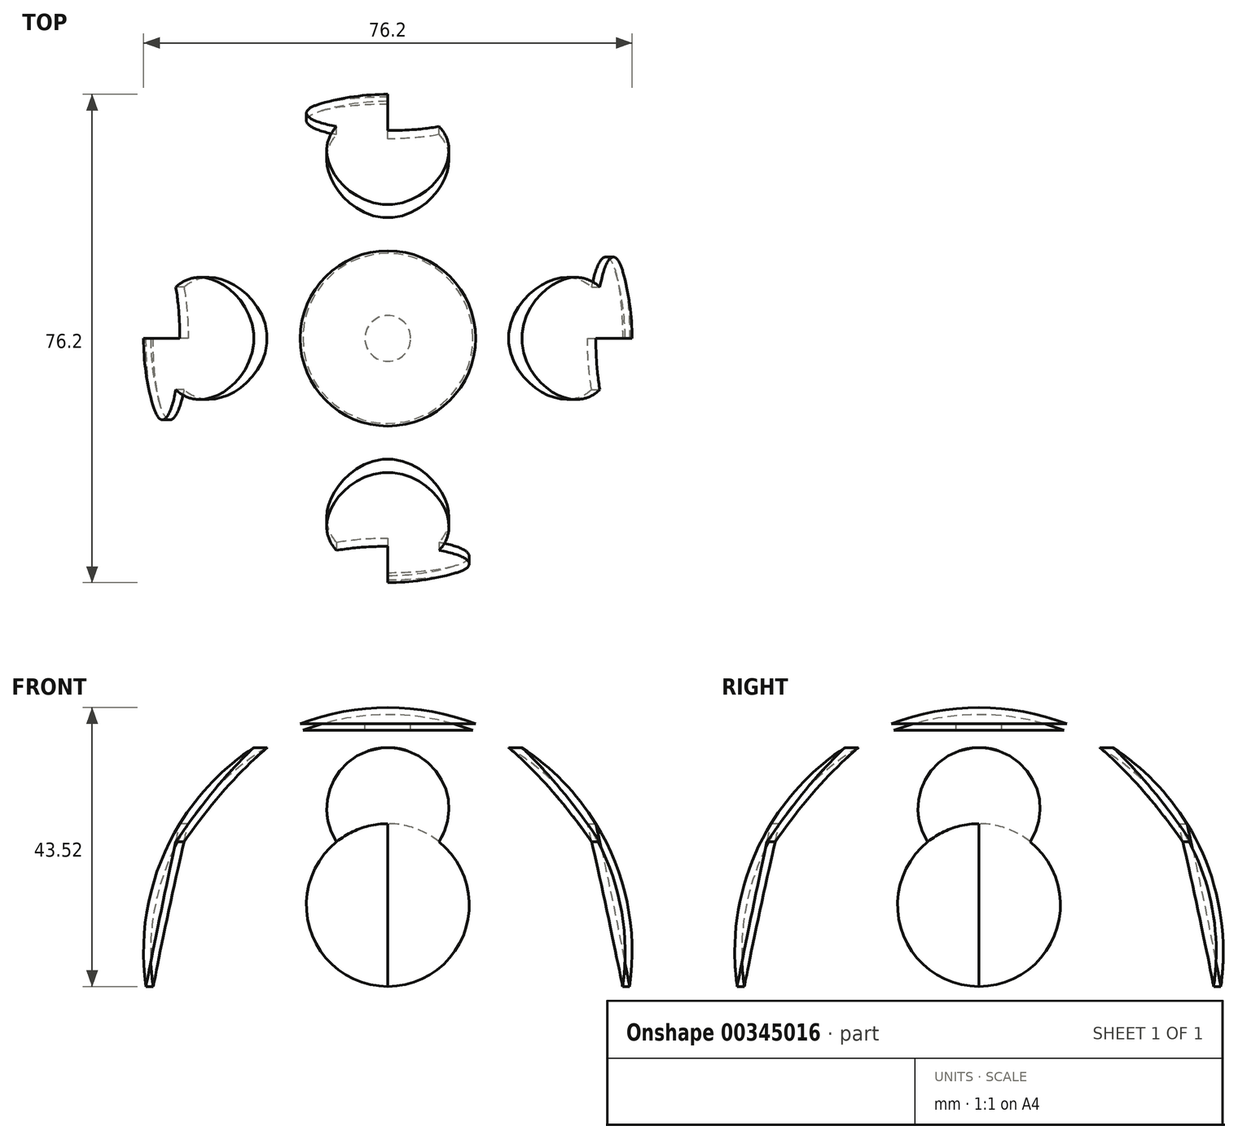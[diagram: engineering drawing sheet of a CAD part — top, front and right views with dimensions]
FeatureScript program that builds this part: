
annotation { "Feature Type Name" : "Feature", "Feature Type Description" : "" }
export const myFeature = defineFeature(function(context is Context, id is Id, definition is map)
    precondition{}
    {
        {
            var Q0;
            Q0=qCreatedBy(makeId("Top.planeOp"),FACE);
            var sketch = newSketch(context, id + "F0", { "sketchPlane" : qUnion([Q0])});
            skArc(sketch, "E0", {"start": v(0, -38.1) * mm, "mid": v(38.1, 0) * mm, "end": v(0, 38.1) * mm});
            skLineSegment(sketch, "E1", {"start": v(0, 38.1) * mm, "end": v(0, -38.1) * mm});
            skSolve(sketch);
        }
        {
            var Q0;
            Q0=makeQuery(id+"F0.imprint","IMPRINT",FACE,{"disambiguationData":[TD([[makeQuery(id+"F0.imprint","IMPRINT",EDGE,{"derivedFrom":sQuery(id+"F0.wireOp",EDGE,"E0")}),1.0]])]});
            var Q1;
            Q1=sQuery(id+"F0.wireOp",EDGE,"E1");
            revolve(context, id + "F1", {"entities" : qUnion([Q0]), "axis" : qUnion([Q1]), "revolveType" : RevolveType.FULL});
        }
        {
            var Q0;
            Q0=qCreatedBy(makeId("Top.planeOp"),FACE);
            cPlane(context, id + "F2", {"entities" : qUnion([Q0]), "cplaneType" : CPlaneType.OFFSET, "offset" : 35.56 * mm, "width" : 152.4 * mm, "height" : 152.4 * mm});
        }
        {
            var Q0;
            Q0=qCreatedBy(id+"F2.planeOp",FACE);
            var sketch = newSketch(context, id + "F3", { "sketchPlane" : qUnion([Q0])});
            skLineSegment(sketch, "E2.bottom", {"start": v(16.51, -16.51) * mm, "end": v(-16.5, -16.51) * mm});
            skLineSegment(sketch, "E2.top", {"start": v(16.5, 16.51) * mm, "end": v(-16.51, 16.51) * mm});
            skLineSegment(sketch, "E2.left", {"start": v(16.51, -16.51) * mm, "end": v(16.5, 16.51) * mm});
            skLineSegment(sketch, "E2.right", {"start": v(-16.51, -16.51) * mm, "end": v(-16.51, 16.51) * mm});
            skPoint(sketch, "E2.middle", {"position": v(0, 0) * mm});
            skSolve(sketch);
        }
        {
            var Q0;
            Q0=makeQuery(id+"F3.imprint","IMPRINT",FACE,{"disambiguationData":[TD([[makeQuery(id+"F3.imprint","IMPRINT",EDGE,{"derivedFrom":sQuery(id+"F3.wireOp",EDGE,"E2.bottom")}),-1.0]])]});
            extrude(context, id + "F4", {"entities" : qUnion([Q0]), "operationType" : NewBodyOperationType.REMOVE, "depth" : 25.4 * mm});
        }
        {
            var Q0;
            Q0=makeQuery(id+"F4.boolean.opBoolean","COPY",FACE,{"derivedFrom":makeQuery(id+"F4.opExtrude","CAP_FACE",FACE,{"disambiguationData":[OSD([sQuery(id+"F3.wireOp",EDGE,"E2.bottom"),sQuery(id+"F3.wireOp",EDGE,"E2.top"),sQuery(id+"F3.wireOp",EDGE,"E2.left"),sQuery(id+"F3.wireOp",EDGE,"E2.right")])],"isStart":true})});
            shell(context, id + "F5", {"entities" : qUnion([Q0]), "thickness" : 1.1 * mm});
        }
        {
            var Q0;
            Q0=qCreatedBy(makeId("Front.planeOp"),FACE);
            cPlane(context, id + "F6", {"entities" : qUnion([Q0]), "cplaneType" : CPlaneType.OFFSET, "offset" : 41.15 * mm, "width" : 152.4 * mm, "height" : 152.4 * mm});
        }
        {
            var Q0;
            Q0=qCreatedBy(id+"F6.planeOp",FACE);
            var sketch = newSketch(context, id + "F7", { "sketchPlane" : qUnion([Q0])});
            skCircle(sketch, "E3", {"center": v(0, 22.33) * mm, "radius": 9.53 * mm});
            skCircle(sketch, "E4", {"center": v(0, 7.28) * mm, "radius": 12.7 * mm});
            skCircle(sketch, "E5", {"center": v(0, -15.5) * mm, "radius": 17.78 * mm});
            skLineSegment(sketch, "E6", {"start": v(0, 22.33) * mm, "end": v(0, 7.28) * mm});
            skLineSegment(sketch, "E7", {"start": v(0, -15.5) * mm, "end": v(0, 7.28) * mm});
            skSolve(sketch);
        }
        {
            var Q0;
            {var subQ0=sQuery(id+"F7.wireOp",EDGE,"E4");var subQ1=sQuery(id+"F7.wireOp",EDGE,"E3");var subQ2=makeQuery(id+"F7.imprint","INTERSECT",VERTEX,{"disambiguationData":[OD(0.0)],"derivedFrom":[subQ1,subQ0]});Q0=makeQuery(id+"F7.imprint","IMPRINT",FACE,{"disambiguationData":[TD([[makeQuery(id+"F7.imprint","IMPRINT",EDGE,{"disambiguationData":[TD([[subQ2,-1.0]])],"derivedFrom":subQ1}),1.0]])]});}
            var Q1;
            {var subQ3=sQuery(id+"F7.wireOp",EDGE,"E3");var subQ6=sQuery(id+"F7.wireOp",EDGE,"E4");var subQ9=makeQuery(id+"F7.imprint","INTERSECT",VERTEX,{"disambiguationData":[OD(0.0)],"derivedFrom":[subQ3,subQ6]});Q1=makeQuery(id+"F7.imprint","IMPRINT",FACE,{"disambiguationData":[TD([[makeQuery(id+"F7.imprint","IMPRINT",EDGE,{"disambiguationData":[TD([[subQ9,-1.0]])],"derivedFrom":subQ3}),-1.0]])]});}
            var Q2;
            {var subQ0=sQuery(id+"F7.wireOp",EDGE,"E4");var subQ1=sQuery(id+"F7.wireOp",EDGE,"E3");var subQ2=makeQuery(id+"F7.imprint","INTERSECT",VERTEX,{"disambiguationData":[OD(1.0)],"derivedFrom":[subQ1,subQ0]});Q2=makeQuery(id+"F7.imprint","IMPRINT",FACE,{"disambiguationData":[TD([[makeQuery(id+"F7.imprint","IMPRINT",EDGE,{"disambiguationData":[TD([[subQ2,1.0]])],"derivedFrom":subQ1}),1.0]])]});}
            var Q3;
            {var subQ1=sQuery(id+"F7.wireOp",EDGE,"E4");var subQ7=sQuery(id+"F7.wireOp",EDGE,"E3");var subQ9=makeQuery(id+"F7.imprint","INTERSECT",VERTEX,{"disambiguationData":[OD(1.0)],"derivedFrom":[subQ7,subQ1]});Q3=makeQuery(id+"F7.imprint","IMPRINT",FACE,{"disambiguationData":[TD([[makeQuery(id+"F7.imprint","IMPRINT",EDGE,{"disambiguationData":[TD([[subQ9,1.0]])],"derivedFrom":subQ7}),-1.0]])]});}
            var Q4;
            {var subQ0=sQuery(id+"F7.wireOp",EDGE,"E5");var subQ1=sQuery(id+"F7.wireOp",EDGE,"E4");var subQ2=makeQuery(id+"F7.imprint","INTERSECT",VERTEX,{"disambiguationData":[OD(0.0)],"derivedFrom":[subQ1,subQ0]});Q4=makeQuery(id+"F7.imprint","IMPRINT",FACE,{"disambiguationData":[TD([[makeQuery(id+"F7.imprint","IMPRINT",EDGE,{"disambiguationData":[TD([[subQ2,-1.0]])],"derivedFrom":subQ1}),1.0]])]});}
            var Q5;
            {var subQ0=sQuery(id+"F7.wireOp",EDGE,"E7");var subQ1=sQuery(id+"F7.wireOp",EDGE,"E4");var subQ2=makeQuery(id+"F7.imprint","INTERSECT",VERTEX,{"derivedFrom":[subQ1,subQ0]});Q5=makeQuery(id+"F7.imprint","IMPRINT",FACE,{"disambiguationData":[TD([[makeQuery(id+"F7.imprint","IMPRINT",EDGE,{"disambiguationData":[TD([[subQ2,-1.0]])],"derivedFrom":subQ1}),1.0]])]});}
            var Q6;
            {var subQ0=sQuery(id+"F7.wireOp",EDGE,"E4");var subQ1=sQuery(id+"F7.wireOp",EDGE,"E3");var subQ2=makeQuery(id+"F7.imprint","INTERSECT",VERTEX,{"disambiguationData":[OD(0.0)],"derivedFrom":[subQ1,subQ0]});Q6=makeQuery(id+"F7.imprint","IMPRINT",FACE,{"disambiguationData":[TD([[makeQuery(id+"F7.imprint","IMPRINT",EDGE,{"disambiguationData":[TD([[subQ2,1.0]])],"derivedFrom":subQ1}),1.0]])]});}
            var Q7;
            {var subQ0=sQuery(id+"F7.wireOp",EDGE,"E5");var subQ1=sQuery(id+"F7.wireOp",EDGE,"E4");var subQ2=makeQuery(id+"F7.imprint","INTERSECT",VERTEX,{"disambiguationData":[OD(0.0)],"derivedFrom":[subQ1,subQ0]});Q7=makeQuery(id+"F7.imprint","IMPRINT",FACE,{"disambiguationData":[TD([[makeQuery(id+"F7.imprint","IMPRINT",EDGE,{"disambiguationData":[TD([[subQ2,-1.0]])],"derivedFrom":subQ1}),-1.0]])]});}
            extrude(context, id + "F8", {"entities" : qUnion([Q0, Q1, Q2, Q3, Q4, Q5, Q6, Q7]), "oppositeDirection" : true, "depth" : 25.4 * mm});
        }
        {
            var Q0;
            Q0=qCreatedBy(makeId("Right.planeOp"),FACE);
            var sketch = newSketch(context, id + "F9", { "sketchPlane" : qUnion([Q0])});
            skPoint(sketch, "E8.start.orphan", {"position": v(0, 45.19) * mm});
            skLineSegment(sketch, "E9", {"start": v(0, 45.19) * mm, "end": v(0, -50.65) * mm, "construction": true});
            skSolve(sketch);
        }
        {
            var Q0;
            Q0=makeQuery(id+"F8.opExtrude","SWEPT_BODY",BODY,{"disambiguationData":[OSD([sQuery(id+"F7.wireOp",EDGE,"E3"),sQuery(id+"F7.wireOp",EDGE,"E4"),sQuery(id+"F7.wireOp",EDGE,"E5")])]});
            var Q1;
            Q1=sQuery(id+"F9.wireOp",EDGE,"E9");
            circularPattern(context, id + "F10", {"entities" : qUnion([Q0]), "axis" : qUnion([Q1]), "angle" : 360 * degree, "instanceCount" : 4, "equalSpace" : true});
        }
        {
            var Q0;
            Q0=makeQuery(id+"F8.opExtrude","SWEPT_BODY",BODY,{"disambiguationData":[OSD([sQuery(id+"F7.wireOp",EDGE,"E3"),sQuery(id+"F7.wireOp",EDGE,"E4"),sQuery(id+"F7.wireOp",EDGE,"E5")])]});
            var Q1;
            Q1=makeQuery(id+"F10.opPattern","COPY",BODY,{"derivedFrom":makeQuery(id+"F8.opExtrude","SWEPT_BODY",BODY,{"disambiguationData":[OSD([sQuery(id+"F7.wireOp",EDGE,"E3"),sQuery(id+"F7.wireOp",EDGE,"E4"),sQuery(id+"F7.wireOp",EDGE,"E5")])]}),"instanceName":"1"});
            var Q2;
            Q2=makeQuery(id+"F10.opPattern","COPY",BODY,{"derivedFrom":makeQuery(id+"F8.opExtrude","SWEPT_BODY",BODY,{"disambiguationData":[OSD([sQuery(id+"F7.wireOp",EDGE,"E3"),sQuery(id+"F7.wireOp",EDGE,"E4"),sQuery(id+"F7.wireOp",EDGE,"E5")])]}),"instanceName":"2"});
            var Q3;
            Q3=makeQuery(id+"F10.opPattern","COPY",BODY,{"derivedFrom":makeQuery(id+"F8.opExtrude","SWEPT_BODY",BODY,{"disambiguationData":[OSD([sQuery(id+"F7.wireOp",EDGE,"E3"),sQuery(id+"F7.wireOp",EDGE,"E4"),sQuery(id+"F7.wireOp",EDGE,"E5")])]}),"instanceName":"3"});
            var Q4;
            Q4=makeQuery(id+"F1.opRevolve","SWEPT_BODY",BODY,{"disambiguationData":[OSD([sQuery(id+"F0.wireOp",EDGE,"E0"),sQuery(id+"F0.wireOp",EDGE,"E1")])]});
            booleanBodies(context, id + "F11", {"operationType" : BooleanOperationType.SUBTRACTION, "tools" : qUnion([Q0, Q1, Q2, Q3]), "targets" : qUnion([Q4])});
        }
        {
            var Q0;
            Q0=makeQuery(id+"F4.boolean.opBoolean","COPY",FACE,{"derivedFrom":makeQuery(id+"F4.opExtrude","CAP_FACE",FACE,{"disambiguationData":[OSD([sQuery(id+"F3.wireOp",EDGE,"E2.bottom"),sQuery(id+"F3.wireOp",EDGE,"E2.top"),sQuery(id+"F3.wireOp",EDGE,"E2.left"),sQuery(id+"F3.wireOp",EDGE,"E2.right")])],"isStart":true})});
            var sketch = newSketch(context, id + "F12", { "sketchPlane" : qUnion([Q0])});
            skCircle(sketch, "E10.0", {"center": v(0, 0) * mm, "radius": 13.68 * mm});
            skCircle(sketch, "E11", {"center": v(0, 0) * mm, "radius": 3.57 * mm});
            skSolve(sketch);
        }
        {
            var Q0;
            Q0 = qSketchRegion(id + "F12", true);
            extrude(context, id + "F13", {"entities" : qUnion([Q0]), "operationType" : NewBodyOperationType.ADD, "oppositeDirection" : true, "depth" : 1.02 * mm});
        }
    });
